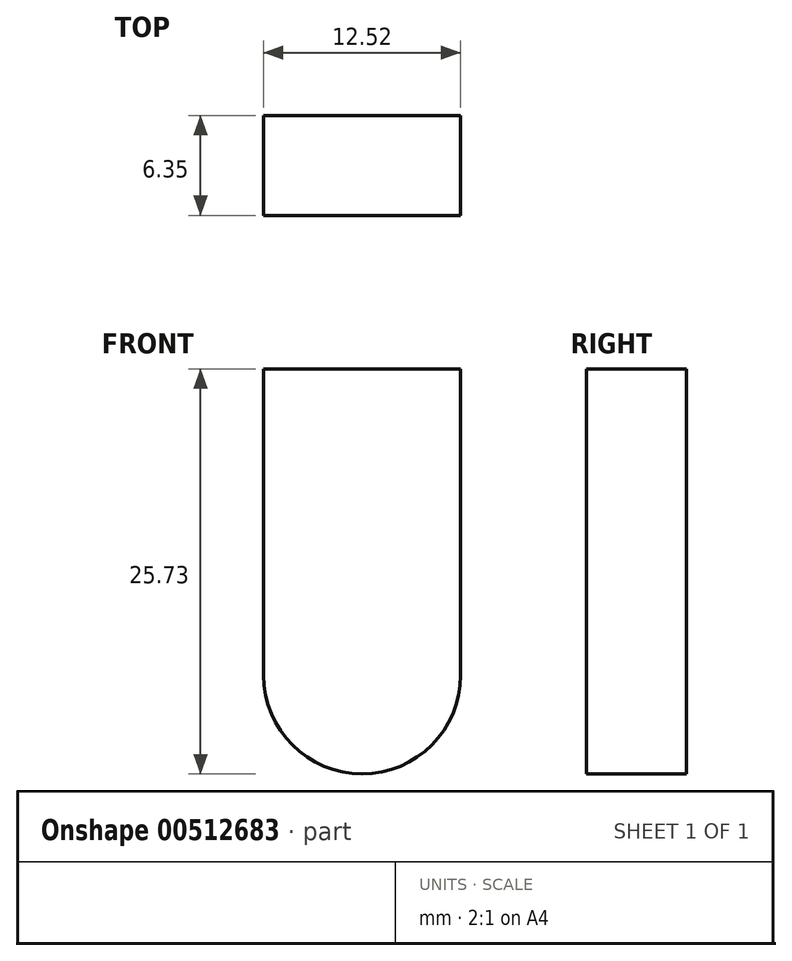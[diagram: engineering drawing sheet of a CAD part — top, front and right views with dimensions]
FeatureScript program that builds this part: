
annotation { "Feature Type Name" : "Feature", "Feature Type Description" : "" }
export const myFeature = defineFeature(function(context is Context, id is Id, definition is map)
    precondition{}
    {
        {
            var Q0;
            Q0=qCreatedBy(makeId("Front.planeOp"),FACE);
            var sketch = newSketch(context, id + "F0", { "sketchPlane" : qUnion([Q0])});
            skLineSegment(sketch, "E0", {"start": v(6.26, 0) * mm, "end": v(6.26, 19.47) * mm});
            skLineSegment(sketch, "E1", {"start": v(6.26, 19.47) * mm, "end": v(-6.26, 19.47) * mm});
            skLineSegment(sketch, "E2", {"start": v(-6.26, 19.47) * mm, "end": v(-6.26, 0) * mm});
            skArc(sketch, "E3", {"start": v(6.26, 0) * mm, "mid": v(0, -6.26) * mm, "end": v(-6.26, 0) * mm});
            skSolve(sketch);
        }
        {
            var Q0;
            Q0 = qSketchRegion(id + "F0", true);
            extrude(context, id + "F1", {"entities" : qUnion([Q0]), "depth" : 6.35 * mm, "offsetDistance" : 25.4 * mm});
        }
    });
